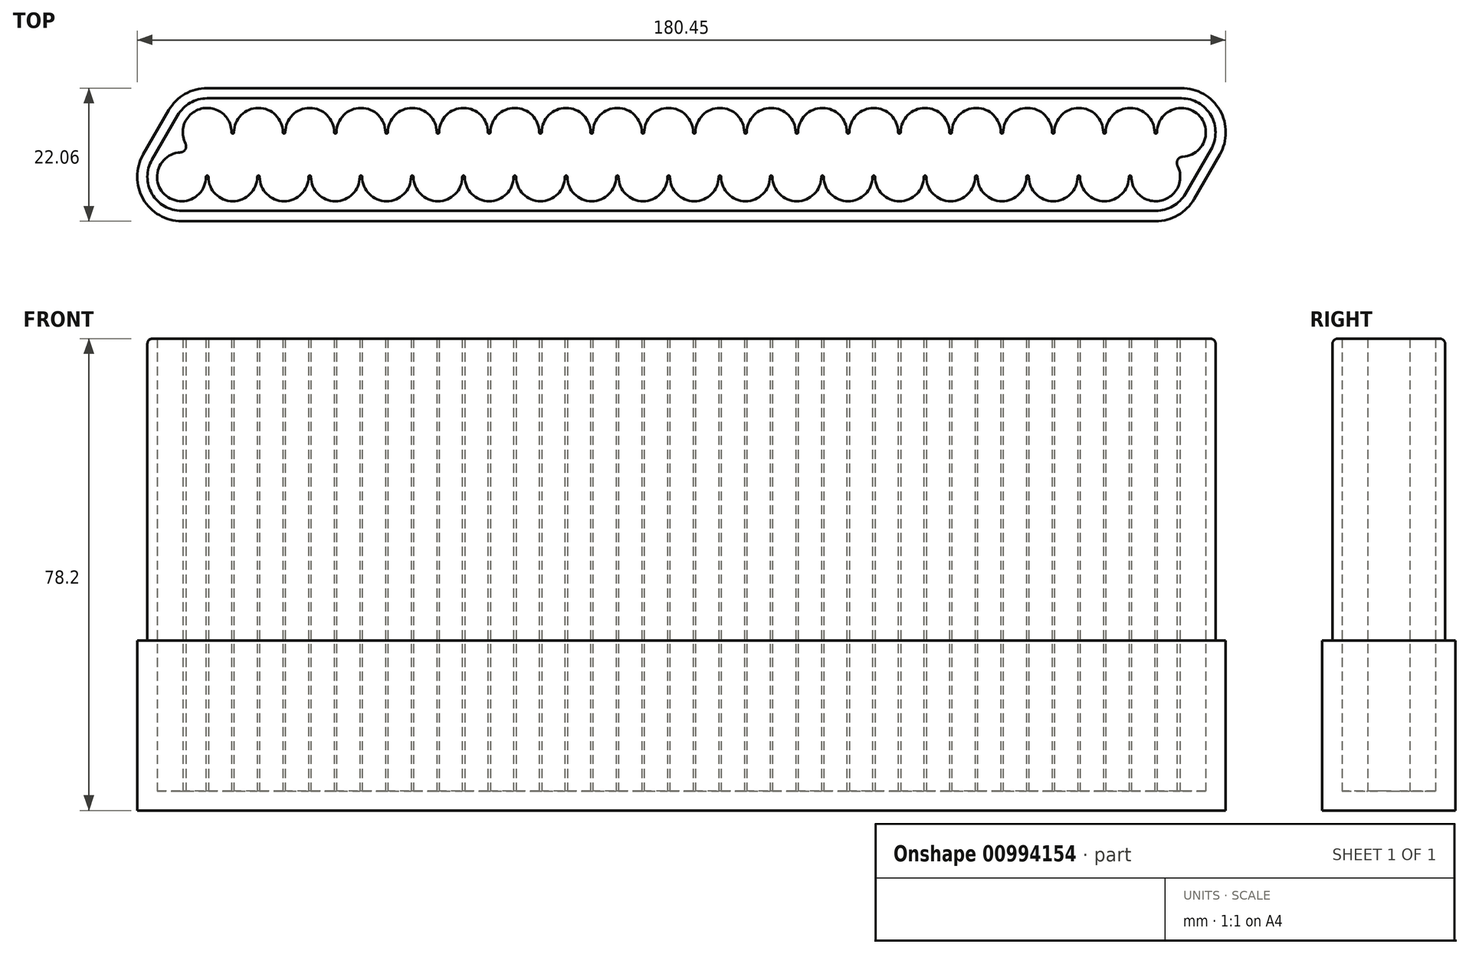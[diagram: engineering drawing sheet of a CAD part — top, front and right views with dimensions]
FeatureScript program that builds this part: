
annotation { "Feature Type Name" : "Feature", "Feature Type Description" : "" }
export const myFeature = defineFeature(function(context is Context, id is Id, definition is map)
    precondition{}
    {
        {
            var Q0;
            Q0=qCreatedBy(makeId("Top.planeOp"),FACE);
            var sketch = newSketch(context, id + "F0", { "sketchPlane" : qUnion([Q0])});
            skCircle(sketch, "E0", {"center": v(0, 0) * mm, "radius": 4.05 * mm});
            skCircle(sketch, "E1.0.1.0", {"center": v(4.25, 7.36) * mm, "radius": 4.05 * mm});
            skCircle(sketch, "E1.1.0.0", {"center": v(8.5, 0) * mm, "radius": 4.05 * mm});
            skCircle(sketch, "E1.1.1.0", {"center": v(12.75, 7.36) * mm, "radius": 4.05 * mm});
            skCircle(sketch, "E1.2.0.0", {"center": v(17, 0) * mm, "radius": 4.05 * mm});
            skCircle(sketch, "E1.2.1.0", {"center": v(21.25, 7.36) * mm, "radius": 4.05 * mm});
            skCircle(sketch, "E1.3.0.0", {"center": v(25.5, 0) * mm, "radius": 4.05 * mm});
            skCircle(sketch, "E1.3.1.0", {"center": v(29.75, 7.36) * mm, "radius": 4.05 * mm});
            skCircle(sketch, "E1.4.0.0", {"center": v(34, 0) * mm, "radius": 4.05 * mm});
            skCircle(sketch, "E1.4.1.0", {"center": v(38.25, 7.36) * mm, "radius": 4.05 * mm});
            skCircle(sketch, "E1.5.0.0", {"center": v(42.5, 0) * mm, "radius": 4.05 * mm});
            skCircle(sketch, "E1.5.1.0", {"center": v(46.75, 7.36) * mm, "radius": 4.05 * mm});
            skCircle(sketch, "E1.6.0.0", {"center": v(51, 0) * mm, "radius": 4.05 * mm});
            skCircle(sketch, "E1.6.1.0", {"center": v(55.25, 7.36) * mm, "radius": 4.05 * mm});
            skCircle(sketch, "E1.7.0.0", {"center": v(59.5, 0) * mm, "radius": 4.05 * mm});
            skCircle(sketch, "E1.7.1.0", {"center": v(63.75, 7.36) * mm, "radius": 4.05 * mm});
            skCircle(sketch, "E1.8.0.0", {"center": v(68, 0) * mm, "radius": 4.05 * mm});
            skCircle(sketch, "E1.8.1.0", {"center": v(72.25, 7.36) * mm, "radius": 4.05 * mm});
            skCircle(sketch, "E1.9.0.0", {"center": v(76.5, 0) * mm, "radius": 4.05 * mm});
            skCircle(sketch, "E1.9.1.0", {"center": v(80.75, 7.36) * mm, "radius": 4.05 * mm});
            skLineSegment(sketch, "E1.direction1", {"start": v(0, 0) * mm, "end": v(8.5, 0) * mm, "construction": true});
            skLineSegment(sketch, "E1.direction2", {"start": v(0, 0) * mm, "end": v(4.25, 7.36) * mm, "construction": true});
            skLineSegment(sketch, "E2", {"start": v(-6.37, 3.67) * mm, "end": v(-2.12, 11.04) * mm});
            skLineSegment(sketch, "E3", {"start": v(-4.9, 2.83) * mm, "end": v(-0.64, 10.19) * mm});
            skLineSegment(sketch, "E4", {"start": v(170.64, 4.54) * mm, "end": v(166.4, -2.83) * mm});
            skLineSegment(sketch, "E5", {"start": v(172.12, 3.69) * mm, "end": v(167.87, -3.68) * mm});
            skLineSegment(sketch, "E6", {"start": v(4.25, 13.01) * mm, "end": v(165.75, 13.01) * mm});
            skLineSegment(sketch, "E7", {"start": v(165.75, 14.71) * mm, "end": v(4.25, 14.71) * mm});
            skLineSegment(sketch, "E8", {"start": v(0, -5.65) * mm, "end": v(161.5, -5.65) * mm});
            skLineSegment(sketch, "E9", {"start": v(161.5, -7.35) * mm, "end": v(0, -7.35) * mm});
            skArc(sketch, "E10", {"start": v(-6.37, 3.67) * mm, "mid": v(-6.37, -3.68) * mm, "end": v(0, -7.35) * mm});
            skArc(sketch, "E11", {"start": v(0, -7.35) * mm, "mid": v(6.37, 3.68) * mm, "end": v(-6.37, 3.67) * mm, "construction": true});
            skArc(sketch, "E12", {"start": v(0, -5.65) * mm, "mid": v(4.9, 2.82) * mm, "end": v(-4.9, 2.83) * mm, "construction": true});
            skArc(sketch, "E13", {"start": v(-4.9, 2.83) * mm, "mid": v(-4.9, -2.83) * mm, "end": v(0, -5.65) * mm});
            skArc(sketch, "E14", {"start": v(4.25, 13.01) * mm, "mid": v(1.43, 12.25) * mm, "end": v(-0.64, 10.19) * mm});
            skArc(sketch, "E15", {"start": v(-0.64, 10.19) * mm, "mid": v(7.08, 2.47) * mm, "end": v(4.25, 13.01) * mm, "construction": true});
            skArc(sketch, "E16", {"start": v(-2.12, 11.04) * mm, "mid": v(7.93, 1) * mm, "end": v(4.25, 14.71) * mm, "construction": true});
            skArc(sketch, "E17", {"start": v(4.25, 14.71) * mm, "mid": v(0.58, 13.73) * mm, "end": v(-2.12, 11.04) * mm});
            skArc(sketch, "E18", {"start": v(165.75, 14.71) * mm, "mid": v(159.38, 3.69) * mm, "end": v(172.12, 3.69) * mm, "construction": true});
            skArc(sketch, "E19", {"start": v(172.12, 3.69) * mm, "mid": v(172.12, 11.04) * mm, "end": v(165.75, 14.71) * mm});
            skArc(sketch, "E20", {"start": v(170.64, 4.54) * mm, "mid": v(170.64, 10.19) * mm, "end": v(165.75, 13.01) * mm});
            skArc(sketch, "E21", {"start": v(165.75, 13.01) * mm, "mid": v(160.86, 4.54) * mm, "end": v(170.64, 4.54) * mm, "construction": true});
            skArc(sketch, "E22", {"start": v(167.87, -3.68) * mm, "mid": v(157.83, 6.37) * mm, "end": v(161.5, -7.35) * mm, "construction": true});
            skArc(sketch, "E23", {"start": v(161.5, -7.35) * mm, "mid": v(165.17, -6.37) * mm, "end": v(167.87, -3.68) * mm});
            skArc(sketch, "E24", {"start": v(161.5, -5.65) * mm, "mid": v(164.32, -4.9) * mm, "end": v(166.4, -2.83) * mm});
            skArc(sketch, "E25", {"start": v(166.4, -2.82) * mm, "mid": v(158.67, 4.9) * mm, "end": v(161.5, -5.65) * mm, "construction": true});
            skArc(sketch, "E26", {"start": v(4.45, 0) * mm, "mid": v(4.25, 0.2) * mm, "end": v(4.05, 0) * mm});
            skArc(sketch, "E27", {"start": v(4.05, 0) * mm, "mid": v(4.25, -0.2) * mm, "end": v(4.45, 0) * mm});
            skArc(sketch, "E28.0.1.0", {"start": v(8.7, 7.36) * mm, "mid": v(8.5, 7.56) * mm, "end": v(8.3, 7.36) * mm});
            skArc(sketch, "E28.0.1.1", {"start": v(8.3, 7.36) * mm, "mid": v(8.5, 7.16) * mm, "end": v(8.7, 7.36) * mm});
            skArc(sketch, "E28.1.0.0", {"start": v(12.95, 0) * mm, "mid": v(12.75, 0.2) * mm, "end": v(12.55, 0) * mm});
            skArc(sketch, "E28.1.0.1", {"start": v(12.55, 0) * mm, "mid": v(12.75, -0.2) * mm, "end": v(12.95, 0) * mm});
            skArc(sketch, "E28.1.1.0", {"start": v(17.2, 7.36) * mm, "mid": v(17, 7.56) * mm, "end": v(16.8, 7.36) * mm});
            skArc(sketch, "E28.1.1.1", {"start": v(16.8, 7.36) * mm, "mid": v(17, 7.16) * mm, "end": v(17.2, 7.36) * mm});
            skArc(sketch, "E28.2.0.0", {"start": v(21.45, 0) * mm, "mid": v(21.25, 0.2) * mm, "end": v(21.05, 0) * mm});
            skArc(sketch, "E28.2.0.1", {"start": v(21.05, 0) * mm, "mid": v(21.25, -0.2) * mm, "end": v(21.45, 0) * mm});
            skArc(sketch, "E28.2.1.0", {"start": v(25.7, 7.36) * mm, "mid": v(25.5, 7.56) * mm, "end": v(25.3, 7.36) * mm});
            skArc(sketch, "E28.2.1.1", {"start": v(25.3, 7.36) * mm, "mid": v(25.5, 7.16) * mm, "end": v(25.7, 7.36) * mm});
            skLineSegment(sketch, "E28.direction1", {"start": v(4.25, 0) * mm, "end": v(12.75, 0) * mm, "construction": true});
            skLineSegment(sketch, "E28.direction2", {"start": v(4.25, 0) * mm, "end": v(8.5, 7.36) * mm, "construction": true});
            skCircle(sketch, "E29.0.10.0", {"center": v(85, 0) * mm, "radius": 4.05 * mm});
            skCircle(sketch, "E29.0.10.1", {"center": v(89.25, 7.36) * mm, "radius": 4.05 * mm});
            skCircle(sketch, "E29.0.11.0", {"center": v(93.5, 0) * mm, "radius": 4.05 * mm});
            skCircle(sketch, "E29.0.11.1", {"center": v(97.75, 7.36) * mm, "radius": 4.05 * mm});
            skCircle(sketch, "E29.0.12.0", {"center": v(102, 0) * mm, "radius": 4.05 * mm});
            skCircle(sketch, "E29.0.12.1", {"center": v(106.25, 7.36) * mm, "radius": 4.05 * mm});
            skCircle(sketch, "E29.0.13.0", {"center": v(110.5, 0) * mm, "radius": 4.05 * mm});
            skCircle(sketch, "E29.0.13.1", {"center": v(114.75, 7.36) * mm, "radius": 4.05 * mm});
            skCircle(sketch, "E29.0.14.0", {"center": v(119, 0) * mm, "radius": 4.05 * mm});
            skCircle(sketch, "E29.0.14.1", {"center": v(123.25, 7.36) * mm, "radius": 4.05 * mm});
            skCircle(sketch, "E29.0.15.0", {"center": v(127.5, 0) * mm, "radius": 4.05 * mm});
            skCircle(sketch, "E29.0.15.1", {"center": v(131.75, 7.36) * mm, "radius": 4.05 * mm});
            skCircle(sketch, "E29.0.16.0", {"center": v(136, 0) * mm, "radius": 4.05 * mm});
            skCircle(sketch, "E29.0.16.1", {"center": v(140.25, 7.36) * mm, "radius": 4.05 * mm});
            skCircle(sketch, "E29.0.17.0", {"center": v(144.5, 0) * mm, "radius": 4.05 * mm});
            skCircle(sketch, "E29.0.17.1", {"center": v(148.75, 7.36) * mm, "radius": 4.05 * mm});
            skCircle(sketch, "E29.0.18.0", {"center": v(153, 0) * mm, "radius": 4.05 * mm});
            skCircle(sketch, "E29.0.18.1", {"center": v(157.25, 7.36) * mm, "radius": 4.05 * mm});
            skCircle(sketch, "E29.0.19.0", {"center": v(161.5, 0) * mm, "radius": 4.05 * mm});
            skCircle(sketch, "E29.0.19.1", {"center": v(165.75, 7.36) * mm, "radius": 4.05 * mm});
            skArc(sketch, "E30.0.3.0", {"start": v(29.95, 0) * mm, "mid": v(29.75, 0.2) * mm, "end": v(29.55, 0) * mm});
            skArc(sketch, "E30.4.3.0", {"start": v(29.55, 0) * mm, "mid": v(29.75, -0.2) * mm, "end": v(29.95, 0) * mm});
            skArc(sketch, "E30.0.3.1", {"start": v(34.2, 7.36) * mm, "mid": v(34, 7.56) * mm, "end": v(33.8, 7.36) * mm});
            skArc(sketch, "E30.4.3.1", {"start": v(33.8, 7.36) * mm, "mid": v(34, 7.16) * mm, "end": v(34.2, 7.36) * mm});
            skArc(sketch, "E30.0.4.0", {"start": v(38.45, 0) * mm, "mid": v(38.25, 0.2) * mm, "end": v(38.05, 0) * mm});
            skArc(sketch, "E30.4.4.0", {"start": v(38.05, 0) * mm, "mid": v(38.25, -0.2) * mm, "end": v(38.45, 0) * mm});
            skArc(sketch, "E30.0.4.1", {"start": v(42.7, 7.36) * mm, "mid": v(42.5, 7.56) * mm, "end": v(42.3, 7.36) * mm});
            skArc(sketch, "E30.4.4.1", {"start": v(42.3, 7.36) * mm, "mid": v(42.5, 7.16) * mm, "end": v(42.7, 7.36) * mm});
            skArc(sketch, "E30.0.5.0", {"start": v(46.95, 0) * mm, "mid": v(46.75, 0.2) * mm, "end": v(46.55, 0) * mm});
            skArc(sketch, "E30.4.5.0", {"start": v(46.55, 0) * mm, "mid": v(46.75, -0.2) * mm, "end": v(46.95, 0) * mm});
            skArc(sketch, "E30.0.5.1", {"start": v(51.2, 7.36) * mm, "mid": v(51, 7.56) * mm, "end": v(50.8, 7.36) * mm});
            skArc(sketch, "E30.4.5.1", {"start": v(50.8, 7.36) * mm, "mid": v(51, 7.16) * mm, "end": v(51.2, 7.36) * mm});
            skArc(sketch, "E30.0.6.0", {"start": v(55.45, 0) * mm, "mid": v(55.25, 0.2) * mm, "end": v(55.05, 0) * mm});
            skArc(sketch, "E30.4.6.0", {"start": v(55.05, 0) * mm, "mid": v(55.25, -0.2) * mm, "end": v(55.45, 0) * mm});
            skArc(sketch, "E30.0.6.1", {"start": v(59.7, 7.36) * mm, "mid": v(59.5, 7.56) * mm, "end": v(59.3, 7.36) * mm});
            skArc(sketch, "E30.4.6.1", {"start": v(59.3, 7.36) * mm, "mid": v(59.5, 7.16) * mm, "end": v(59.7, 7.36) * mm});
            skArc(sketch, "E30.0.7.0", {"start": v(63.95, 0) * mm, "mid": v(63.75, 0.2) * mm, "end": v(63.55, 0) * mm});
            skArc(sketch, "E30.4.7.0", {"start": v(63.55, 0) * mm, "mid": v(63.75, -0.2) * mm, "end": v(63.95, 0) * mm});
            skArc(sketch, "E30.0.7.1", {"start": v(68.2, 7.36) * mm, "mid": v(68, 7.56) * mm, "end": v(67.8, 7.36) * mm});
            skArc(sketch, "E30.4.7.1", {"start": v(67.8, 7.36) * mm, "mid": v(68, 7.16) * mm, "end": v(68.2, 7.36) * mm});
            skArc(sketch, "E30.0.8.0", {"start": v(72.45, 0) * mm, "mid": v(72.25, 0.2) * mm, "end": v(72.05, 0) * mm});
            skArc(sketch, "E30.4.8.0", {"start": v(72.05, 0) * mm, "mid": v(72.25, -0.2) * mm, "end": v(72.45, 0) * mm});
            skArc(sketch, "E30.0.8.1", {"start": v(76.7, 7.36) * mm, "mid": v(76.5, 7.56) * mm, "end": v(76.3, 7.36) * mm});
            skArc(sketch, "E30.4.8.1", {"start": v(76.3, 7.36) * mm, "mid": v(76.5, 7.16) * mm, "end": v(76.7, 7.36) * mm});
            skArc(sketch, "E30.0.9.0", {"start": v(80.95, 0) * mm, "mid": v(80.75, 0.2) * mm, "end": v(80.55, 0) * mm});
            skArc(sketch, "E30.4.9.0", {"start": v(80.55, 0) * mm, "mid": v(80.75, -0.2) * mm, "end": v(80.95, 0) * mm});
            skArc(sketch, "E30.0.9.1", {"start": v(85.2, 7.36) * mm, "mid": v(85, 7.56) * mm, "end": v(84.8, 7.36) * mm});
            skArc(sketch, "E30.4.9.1", {"start": v(84.8, 7.36) * mm, "mid": v(85, 7.16) * mm, "end": v(85.2, 7.36) * mm});
            skArc(sketch, "E30.0.10.0", {"start": v(89.45, 0) * mm, "mid": v(89.25, 0.2) * mm, "end": v(89.05, 0) * mm});
            skArc(sketch, "E30.4.10.0", {"start": v(89.05, 0) * mm, "mid": v(89.25, -0.2) * mm, "end": v(89.45, 0) * mm});
            skArc(sketch, "E30.0.10.1", {"start": v(93.7, 7.36) * mm, "mid": v(93.5, 7.56) * mm, "end": v(93.3, 7.36) * mm});
            skArc(sketch, "E30.4.10.1", {"start": v(93.3, 7.36) * mm, "mid": v(93.5, 7.16) * mm, "end": v(93.7, 7.36) * mm});
            skArc(sketch, "E30.0.11.0", {"start": v(97.95, 0) * mm, "mid": v(97.75, 0.2) * mm, "end": v(97.55, 0) * mm});
            skArc(sketch, "E30.4.11.0", {"start": v(97.55, 0) * mm, "mid": v(97.75, -0.2) * mm, "end": v(97.95, 0) * mm});
            skArc(sketch, "E30.0.11.1", {"start": v(102.2, 7.36) * mm, "mid": v(102, 7.56) * mm, "end": v(101.8, 7.36) * mm});
            skArc(sketch, "E30.4.11.1", {"start": v(101.8, 7.36) * mm, "mid": v(102, 7.16) * mm, "end": v(102.2, 7.36) * mm});
            skArc(sketch, "E30.0.12.0", {"start": v(106.45, 0) * mm, "mid": v(106.25, 0.2) * mm, "end": v(106.05, 0) * mm});
            skArc(sketch, "E30.4.12.0", {"start": v(106.05, 0) * mm, "mid": v(106.25, -0.2) * mm, "end": v(106.45, 0) * mm});
            skArc(sketch, "E30.0.12.1", {"start": v(110.7, 7.36) * mm, "mid": v(110.5, 7.56) * mm, "end": v(110.3, 7.36) * mm});
            skArc(sketch, "E30.4.12.1", {"start": v(110.3, 7.36) * mm, "mid": v(110.5, 7.16) * mm, "end": v(110.7, 7.36) * mm});
            skArc(sketch, "E30.0.13.0", {"start": v(114.95, 0) * mm, "mid": v(114.75, 0.2) * mm, "end": v(114.55, 0) * mm});
            skArc(sketch, "E30.4.13.0", {"start": v(114.55, 0) * mm, "mid": v(114.75, -0.2) * mm, "end": v(114.95, 0) * mm});
            skArc(sketch, "E30.0.13.1", {"start": v(119.2, 7.36) * mm, "mid": v(119, 7.56) * mm, "end": v(118.8, 7.36) * mm});
            skArc(sketch, "E30.4.13.1", {"start": v(118.8, 7.36) * mm, "mid": v(119, 7.16) * mm, "end": v(119.2, 7.36) * mm});
            skArc(sketch, "E30.0.14.0", {"start": v(123.45, 0) * mm, "mid": v(123.25, 0.2) * mm, "end": v(123.05, 0) * mm});
            skArc(sketch, "E30.4.14.0", {"start": v(123.05, 0) * mm, "mid": v(123.25, -0.2) * mm, "end": v(123.45, 0) * mm});
            skArc(sketch, "E30.0.14.1", {"start": v(127.7, 7.36) * mm, "mid": v(127.5, 7.56) * mm, "end": v(127.3, 7.36) * mm});
            skArc(sketch, "E30.4.14.1", {"start": v(127.3, 7.36) * mm, "mid": v(127.5, 7.16) * mm, "end": v(127.7, 7.36) * mm});
            skArc(sketch, "E30.0.15.0", {"start": v(131.95, 0) * mm, "mid": v(131.75, 0.2) * mm, "end": v(131.55, 0) * mm});
            skArc(sketch, "E30.4.15.0", {"start": v(131.55, 0) * mm, "mid": v(131.75, -0.2) * mm, "end": v(131.95, 0) * mm});
            skArc(sketch, "E30.0.15.1", {"start": v(136.2, 7.36) * mm, "mid": v(136, 7.56) * mm, "end": v(135.8, 7.36) * mm});
            skArc(sketch, "E30.4.15.1", {"start": v(135.8, 7.36) * mm, "mid": v(136, 7.16) * mm, "end": v(136.2, 7.36) * mm});
            skArc(sketch, "E30.0.16.0", {"start": v(140.45, 0) * mm, "mid": v(140.25, 0.2) * mm, "end": v(140.05, 0) * mm});
            skArc(sketch, "E30.4.16.0", {"start": v(140.05, 0) * mm, "mid": v(140.25, -0.2) * mm, "end": v(140.45, 0) * mm});
            skArc(sketch, "E30.0.16.1", {"start": v(144.7, 7.36) * mm, "mid": v(144.5, 7.56) * mm, "end": v(144.3, 7.36) * mm});
            skArc(sketch, "E30.4.16.1", {"start": v(144.3, 7.36) * mm, "mid": v(144.5, 7.16) * mm, "end": v(144.7, 7.36) * mm});
            skArc(sketch, "E30.0.17.0", {"start": v(148.95, 0) * mm, "mid": v(148.75, 0.2) * mm, "end": v(148.55, 0) * mm});
            skArc(sketch, "E30.4.17.0", {"start": v(148.55, 0) * mm, "mid": v(148.75, -0.2) * mm, "end": v(148.95, 0) * mm});
            skArc(sketch, "E30.0.17.1", {"start": v(153.2, 7.36) * mm, "mid": v(153, 7.56) * mm, "end": v(152.8, 7.36) * mm});
            skArc(sketch, "E30.4.17.1", {"start": v(152.8, 7.36) * mm, "mid": v(153, 7.16) * mm, "end": v(153.2, 7.36) * mm});
            skArc(sketch, "E30.0.18.0", {"start": v(157.45, 0) * mm, "mid": v(157.25, 0.2) * mm, "end": v(157.05, 0) * mm});
            skArc(sketch, "E30.4.18.0", {"start": v(157.05, 0) * mm, "mid": v(157.25, -0.2) * mm, "end": v(157.45, 0) * mm});
            skArc(sketch, "E30.0.18.1", {"start": v(161.7, 7.36) * mm, "mid": v(161.5, 7.56) * mm, "end": v(161.3, 7.36) * mm});
            skArc(sketch, "E30.4.18.1", {"start": v(161.3, 7.36) * mm, "mid": v(161.5, 7.16) * mm, "end": v(161.7, 7.36) * mm});
            skLineSegment(sketch, "E31", {"start": v(161.5, 0) * mm, "end": v(165.75, 7.36) * mm, "construction": true});
            skLineSegment(sketch, "E32", {"start": v(2.13, 3.68) * mm, "end": v(-0.24, 5.04) * mm, "construction": true});
            skArc(sketch, "E33", {"start": v(0.65, 5.5) * mm, "mid": v(-1.1, 5.54) * mm, "end": v(-0.2, 4.05) * mm, "construction": true});
            skArc(sketch, "E34", {"start": v(-0.2, 4.05) * mm, "mid": v(0.63, 4.54) * mm, "end": v(0.65, 5.5) * mm});
            skLineSegment(sketch, "E35", {"start": v(163.62, 3.68) * mm, "end": v(165.99, 2.32) * mm, "construction": true});
            skArc(sketch, "E36", {"start": v(165.94, 3.32) * mm, "mid": v(165.12, 2.82) * mm, "end": v(165.1, 1.86) * mm});
            skArc(sketch, "E37", {"start": v(165.1, 1.86) * mm, "mid": v(166.85, 1.82) * mm, "end": v(165.94, 3.32) * mm, "construction": true});
            skSolve(sketch);
        }
        {
            var Q0;
            Q0=makeQuery(id+"F0.imprint","IMPRINT",FACE,{"disambiguationData":[TD([[makeQuery(id+"F0.imprint","IMPRINT",EDGE,{"derivedFrom":sQuery(id+"F0.wireOp",EDGE,"E3")}),-1.0]])]});
            var Q1;
            Q1=makeQuery(id+"F0.imprint","IMPRINT",FACE,{"disambiguationData":[TD([[makeQuery(id+"F0.imprint","IMPRINT",EDGE,{"derivedFrom":sQuery(id+"F0.wireOp",EDGE,"E26")}),1.0]])]});
            var Q2;
            {var subQ0=sQuery(id+"F0.wireOp",EDGE,"E28.0.1.0");Q2=makeQuery(id+"F0.imprint","IMPRINT",FACE,{"disambiguationData":[TD([[makeQuery(id+"F0.imprint","IMPRINT",EDGE,{"derivedFrom":subQ0}),1.0]])]});}
            var Q3;
            Q3=makeQuery(id+"F0.imprint","IMPRINT",FACE,{"disambiguationData":[TD([[makeQuery(id+"F0.imprint","IMPRINT",EDGE,{"derivedFrom":sQuery(id+"F0.wireOp",EDGE,"E28.1.0.0")}),1.0]])]});
            var Q4;
            Q4=makeQuery(id+"F0.imprint","IMPRINT",FACE,{"disambiguationData":[TD([[makeQuery(id+"F0.imprint","IMPRINT",EDGE,{"derivedFrom":sQuery(id+"F0.wireOp",EDGE,"E28.1.1.0")}),1.0]])]});
            var Q5;
            Q5=makeQuery(id+"F0.imprint","IMPRINT",FACE,{"disambiguationData":[TD([[makeQuery(id+"F0.imprint","IMPRINT",EDGE,{"derivedFrom":sQuery(id+"F0.wireOp",EDGE,"E28.2.0.0")}),1.0]])]});
            var Q6;
            Q6=makeQuery(id+"F0.imprint","IMPRINT",FACE,{"disambiguationData":[TD([[makeQuery(id+"F0.imprint","IMPRINT",EDGE,{"derivedFrom":sQuery(id+"F0.wireOp",EDGE,"E28.2.1.0")}),1.0]])]});
            var Q7;
            Q7=makeQuery(id+"F0.imprint","IMPRINT",FACE,{"disambiguationData":[TD([[makeQuery(id+"F0.imprint","IMPRINT",EDGE,{"derivedFrom":sQuery(id+"F0.wireOp",EDGE,"E30.0.3.0")}),1.0]])]});
            var Q8;
            Q8=makeQuery(id+"F0.imprint","IMPRINT",FACE,{"disambiguationData":[TD([[makeQuery(id+"F0.imprint","IMPRINT",EDGE,{"derivedFrom":sQuery(id+"F0.wireOp",EDGE,"E30.0.3.1")}),1.0]])]});
            var Q9;
            Q9=makeQuery(id+"F0.imprint","IMPRINT",FACE,{"disambiguationData":[TD([[makeQuery(id+"F0.imprint","IMPRINT",EDGE,{"derivedFrom":sQuery(id+"F0.wireOp",EDGE,"E30.0.4.0")}),1.0]])]});
            var Q10;
            Q10=makeQuery(id+"F0.imprint","IMPRINT",FACE,{"disambiguationData":[TD([[makeQuery(id+"F0.imprint","IMPRINT",EDGE,{"derivedFrom":sQuery(id+"F0.wireOp",EDGE,"E30.0.4.1")}),1.0]])]});
            var Q11;
            Q11=makeQuery(id+"F0.imprint","IMPRINT",FACE,{"disambiguationData":[TD([[makeQuery(id+"F0.imprint","IMPRINT",EDGE,{"derivedFrom":sQuery(id+"F0.wireOp",EDGE,"E30.0.5.0")}),1.0]])]});
            var Q12;
            Q12=makeQuery(id+"F0.imprint","IMPRINT",FACE,{"disambiguationData":[TD([[makeQuery(id+"F0.imprint","IMPRINT",EDGE,{"derivedFrom":sQuery(id+"F0.wireOp",EDGE,"E30.0.5.1")}),1.0]])]});
            var Q13;
            Q13=makeQuery(id+"F0.imprint","IMPRINT",FACE,{"disambiguationData":[TD([[makeQuery(id+"F0.imprint","IMPRINT",EDGE,{"derivedFrom":sQuery(id+"F0.wireOp",EDGE,"E30.0.6.0")}),1.0]])]});
            var Q14;
            Q14=makeQuery(id+"F0.imprint","IMPRINT",FACE,{"disambiguationData":[TD([[makeQuery(id+"F0.imprint","IMPRINT",EDGE,{"derivedFrom":sQuery(id+"F0.wireOp",EDGE,"E30.0.6.1")}),1.0]])]});
            var Q15;
            Q15=makeQuery(id+"F0.imprint","IMPRINT",FACE,{"disambiguationData":[TD([[makeQuery(id+"F0.imprint","IMPRINT",EDGE,{"derivedFrom":sQuery(id+"F0.wireOp",EDGE,"E30.0.7.0")}),1.0]])]});
            var Q16;
            Q16=makeQuery(id+"F0.imprint","IMPRINT",FACE,{"disambiguationData":[TD([[makeQuery(id+"F0.imprint","IMPRINT",EDGE,{"derivedFrom":sQuery(id+"F0.wireOp",EDGE,"E30.0.7.1")}),1.0]])]});
            var Q17;
            Q17=makeQuery(id+"F0.imprint","IMPRINT",FACE,{"disambiguationData":[TD([[makeQuery(id+"F0.imprint","IMPRINT",EDGE,{"derivedFrom":sQuery(id+"F0.wireOp",EDGE,"E30.0.8.0")}),1.0]])]});
            var Q18;
            Q18=makeQuery(id+"F0.imprint","IMPRINT",FACE,{"disambiguationData":[TD([[makeQuery(id+"F0.imprint","IMPRINT",EDGE,{"derivedFrom":sQuery(id+"F0.wireOp",EDGE,"E30.0.8.1")}),1.0]])]});
            var Q19;
            Q19=makeQuery(id+"F0.imprint","IMPRINT",FACE,{"disambiguationData":[TD([[makeQuery(id+"F0.imprint","IMPRINT",EDGE,{"derivedFrom":sQuery(id+"F0.wireOp",EDGE,"E30.0.9.0")}),1.0]])]});
            var Q20;
            Q20=makeQuery(id+"F0.imprint","IMPRINT",FACE,{"disambiguationData":[TD([[makeQuery(id+"F0.imprint","IMPRINT",EDGE,{"derivedFrom":sQuery(id+"F0.wireOp",EDGE,"E30.0.9.1")}),1.0]])]});
            var Q21;
            Q21=makeQuery(id+"F0.imprint","IMPRINT",FACE,{"disambiguationData":[TD([[makeQuery(id+"F0.imprint","IMPRINT",EDGE,{"derivedFrom":sQuery(id+"F0.wireOp",EDGE,"E30.0.10.0")}),1.0]])]});
            var Q22;
            Q22=makeQuery(id+"F0.imprint","IMPRINT",FACE,{"disambiguationData":[TD([[makeQuery(id+"F0.imprint","IMPRINT",EDGE,{"derivedFrom":sQuery(id+"F0.wireOp",EDGE,"E30.0.10.1")}),1.0]])]});
            var Q23;
            Q23=makeQuery(id+"F0.imprint","IMPRINT",FACE,{"disambiguationData":[TD([[makeQuery(id+"F0.imprint","IMPRINT",EDGE,{"derivedFrom":sQuery(id+"F0.wireOp",EDGE,"E30.0.11.0")}),1.0]])]});
            var Q24;
            Q24=makeQuery(id+"F0.imprint","IMPRINT",FACE,{"disambiguationData":[TD([[makeQuery(id+"F0.imprint","IMPRINT",EDGE,{"derivedFrom":sQuery(id+"F0.wireOp",EDGE,"E30.0.11.1")}),1.0]])]});
            var Q25;
            Q25=makeQuery(id+"F0.imprint","IMPRINT",FACE,{"disambiguationData":[TD([[makeQuery(id+"F0.imprint","IMPRINT",EDGE,{"derivedFrom":sQuery(id+"F0.wireOp",EDGE,"E30.0.12.0")}),1.0]])]});
            var Q26;
            Q26=makeQuery(id+"F0.imprint","IMPRINT",FACE,{"disambiguationData":[TD([[makeQuery(id+"F0.imprint","IMPRINT",EDGE,{"derivedFrom":sQuery(id+"F0.wireOp",EDGE,"E30.0.12.1")}),1.0]])]});
            var Q27;
            Q27=makeQuery(id+"F0.imprint","IMPRINT",FACE,{"disambiguationData":[TD([[makeQuery(id+"F0.imprint","IMPRINT",EDGE,{"derivedFrom":sQuery(id+"F0.wireOp",EDGE,"E30.0.13.0")}),1.0]])]});
            var Q28;
            Q28=makeQuery(id+"F0.imprint","IMPRINT",FACE,{"disambiguationData":[TD([[makeQuery(id+"F0.imprint","IMPRINT",EDGE,{"derivedFrom":sQuery(id+"F0.wireOp",EDGE,"E30.0.13.1")}),1.0]])]});
            var Q29;
            Q29=makeQuery(id+"F0.imprint","IMPRINT",FACE,{"disambiguationData":[TD([[makeQuery(id+"F0.imprint","IMPRINT",EDGE,{"derivedFrom":sQuery(id+"F0.wireOp",EDGE,"E30.0.14.0")}),1.0]])]});
            var Q30;
            Q30=makeQuery(id+"F0.imprint","IMPRINT",FACE,{"disambiguationData":[TD([[makeQuery(id+"F0.imprint","IMPRINT",EDGE,{"derivedFrom":sQuery(id+"F0.wireOp",EDGE,"E30.0.14.1")}),1.0]])]});
            var Q31;
            Q31=makeQuery(id+"F0.imprint","IMPRINT",FACE,{"disambiguationData":[TD([[makeQuery(id+"F0.imprint","IMPRINT",EDGE,{"derivedFrom":sQuery(id+"F0.wireOp",EDGE,"E30.0.15.0")}),1.0]])]});
            var Q32;
            Q32=makeQuery(id+"F0.imprint","IMPRINT",FACE,{"disambiguationData":[TD([[makeQuery(id+"F0.imprint","IMPRINT",EDGE,{"derivedFrom":sQuery(id+"F0.wireOp",EDGE,"E30.0.15.1")}),1.0]])]});
            var Q33;
            Q33=makeQuery(id+"F0.imprint","IMPRINT",FACE,{"disambiguationData":[TD([[makeQuery(id+"F0.imprint","IMPRINT",EDGE,{"derivedFrom":sQuery(id+"F0.wireOp",EDGE,"E30.0.16.0")}),1.0]])]});
            var Q34;
            Q34=makeQuery(id+"F0.imprint","IMPRINT",FACE,{"disambiguationData":[TD([[makeQuery(id+"F0.imprint","IMPRINT",EDGE,{"derivedFrom":sQuery(id+"F0.wireOp",EDGE,"E30.0.16.1")}),1.0]])]});
            var Q35;
            Q35=makeQuery(id+"F0.imprint","IMPRINT",FACE,{"disambiguationData":[TD([[makeQuery(id+"F0.imprint","IMPRINT",EDGE,{"derivedFrom":sQuery(id+"F0.wireOp",EDGE,"E30.0.17.0")}),1.0]])]});
            var Q36;
            Q36=makeQuery(id+"F0.imprint","IMPRINT",FACE,{"disambiguationData":[TD([[makeQuery(id+"F0.imprint","IMPRINT",EDGE,{"derivedFrom":sQuery(id+"F0.wireOp",EDGE,"E30.0.17.1")}),1.0]])]});
            var Q37;
            Q37=makeQuery(id+"F0.imprint","IMPRINT",FACE,{"disambiguationData":[TD([[makeQuery(id+"F0.imprint","IMPRINT",EDGE,{"derivedFrom":sQuery(id+"F0.wireOp",EDGE,"E30.0.18.0")}),1.0]])]});
            var Q38;
            Q38=makeQuery(id+"F0.imprint","IMPRINT",FACE,{"disambiguationData":[TD([[makeQuery(id+"F0.imprint","IMPRINT",EDGE,{"derivedFrom":sQuery(id+"F0.wireOp",EDGE,"E30.0.18.1")}),1.0]])]});
            extrude(context, id + "F1", {"entities" : qUnion([Q0, Q1, Q2, Q3, Q4, Q5, Q6, Q7, Q8, Q9, Q10, Q11, Q12, Q13, Q14, Q15, Q16, Q17, Q18, Q19, Q20, Q21, Q22, Q23, Q24, Q25, Q26, Q27, Q28, Q29, Q30, Q31, Q32, Q33, Q34, Q35, Q36, Q37, Q38]), "depth" : 75 * mm, "offsetDistance" : 25 * mm});
        }
        {
            var Q0;
            Q0=makeQuery(id+"F0.imprint","IMPRINT",FACE,{"disambiguationData":[TD([[makeQuery(id+"F0.imprint","IMPRINT",EDGE,{"derivedFrom":sQuery(id+"F0.wireOp",EDGE,"a81a9441-913f-4e04-ae89-87223a70fdbe.0")}),1.0]])]});
            var Q1;
            Q1=makeQuery(id+"F0.imprint","IMPRINT",FACE,{"disambiguationData":[TD([[makeQuery(id+"F0.imprint","IMPRINT",EDGE,{"derivedFrom":sQuery(id+"F0.wireOp",EDGE,"E2")}),-1.0]])]});
            extrude(context, id + "F2", {"entities" : qUnion([Q0, Q1]), "operationType" : NewBodyOperationType.ADD, "depth" : 25 * mm, "offsetDistance" : 25 * mm});
        }
        {
            var Q0;
            Q0 = qSketchRegion(id + "F0", true);
            var Q1;
            Q1=makeQuery(id+"F0.imprint","IMPRINT",FACE,{"disambiguationData":[TD([[makeQuery(id+"F0.imprint","IMPRINT",EDGE,{"derivedFrom":sQuery(id+"F0.wireOp",EDGE,"E3")}),-1.0]])]});
            var Q2;
            {var subQ50=sQuery(id+"F0.wireOp",EDGE,"f7ba4f12-d8f7-416d-8bb5-9bc70fdc84212");Q2=makeQuery(id+"F0.imprint","IMPRINT",FACE,{"disambiguationData":[TD([[makeQuery(id+"F0.imprint","IMPRINT",EDGE,{"derivedFrom":subQ50}),-1.0]])]});}
            var Q3;
            {var subQ0=sQuery(id+"F0.wireOp",EDGE,"E0");var subQ1=makeQuery(id+"F0.imprint","INTERSECT",VERTEX,{"derivedFrom":[subQ0,sQuery(id+"F0.wireOp",EDGE,"f7ba4f12-d8f7-416d-8bb5-9bc70fdc84212")]});Q3=makeQuery(id+"F0.imprint","IMPRINT",FACE,{"disambiguationData":[TD([[makeQuery(id+"F0.imprint","IMPRINT",EDGE,{"disambiguationData":[TD([[subQ1,1.0]])],"derivedFrom":subQ0}),1.0]])]});}
            var Q4;
            {var subQ0=sQuery(id+"F0.wireOp",EDGE,"E1.0.1.0");var subQ1=makeQuery(id+"F0.imprint","INTERSECT",VERTEX,{"derivedFrom":[subQ0,sQuery(id+"F0.wireOp",EDGE,"f7ba4f12-d8f7-416d-8bb5-9bc70fdc84212")]});Q4=makeQuery(id+"F0.imprint","IMPRINT",FACE,{"disambiguationData":[TD([[makeQuery(id+"F0.imprint","IMPRINT",EDGE,{"disambiguationData":[TD([[subQ1,1.0]])],"derivedFrom":subQ0}),1.0]])]});}
            var Q5;
            {var subQ0=sQuery(id+"F0.wireOp",EDGE,"E1.1.0.0");var subQ1=makeQuery(id+"F0.imprint","INTERSECT",VERTEX,{"derivedFrom":[subQ0,sQuery(id+"F0.wireOp",EDGE,"E26")]});Q5=makeQuery(id+"F0.imprint","IMPRINT",FACE,{"disambiguationData":[TD([[makeQuery(id+"F0.imprint","IMPRINT",EDGE,{"disambiguationData":[TD([[subQ1,1.0]])],"derivedFrom":subQ0}),1.0]])]});}
            var Q6;
            {var subQ0=sQuery(id+"F0.wireOp",EDGE,"E1.1.1.0");var subQ1=makeQuery(id+"F0.imprint","INTERSECT",VERTEX,{"derivedFrom":[subQ0,sQuery(id+"F0.wireOp",EDGE,"E28.0.1.1")]});Q6=makeQuery(id+"F0.imprint","IMPRINT",FACE,{"disambiguationData":[TD([[makeQuery(id+"F0.imprint","IMPRINT",EDGE,{"disambiguationData":[TD([[subQ1,1.0]])],"derivedFrom":subQ0}),1.0]])]});}
            var Q7;
            {var subQ0=sQuery(id+"F0.wireOp",EDGE,"E1.2.0.0");var subQ1=makeQuery(id+"F0.imprint","INTERSECT",VERTEX,{"derivedFrom":[subQ0,sQuery(id+"F0.wireOp",EDGE,"E28.1.0.0")]});Q7=makeQuery(id+"F0.imprint","IMPRINT",FACE,{"disambiguationData":[TD([[makeQuery(id+"F0.imprint","IMPRINT",EDGE,{"disambiguationData":[TD([[subQ1,1.0]])],"derivedFrom":subQ0}),1.0]])]});}
            var Q8;
            {var subQ0=sQuery(id+"F0.wireOp",EDGE,"E1.2.1.0");var subQ1=makeQuery(id+"F0.imprint","INTERSECT",VERTEX,{"derivedFrom":[subQ0,sQuery(id+"F0.wireOp",EDGE,"E28.1.1.1")]});Q8=makeQuery(id+"F0.imprint","IMPRINT",FACE,{"disambiguationData":[TD([[makeQuery(id+"F0.imprint","IMPRINT",EDGE,{"disambiguationData":[TD([[subQ1,1.0]])],"derivedFrom":subQ0}),1.0]])]});}
            var Q9;
            {var subQ0=sQuery(id+"F0.wireOp",EDGE,"E1.3.0.0");var subQ1=makeQuery(id+"F0.imprint","INTERSECT",VERTEX,{"derivedFrom":[subQ0,sQuery(id+"F0.wireOp",EDGE,"E28.2.0.0")]});Q9=makeQuery(id+"F0.imprint","IMPRINT",FACE,{"disambiguationData":[TD([[makeQuery(id+"F0.imprint","IMPRINT",EDGE,{"disambiguationData":[TD([[subQ1,1.0]])],"derivedFrom":subQ0}),1.0]])]});}
            var Q10;
            {var subQ0=sQuery(id+"F0.wireOp",EDGE,"E1.3.1.0");var subQ1=makeQuery(id+"F0.imprint","INTERSECT",VERTEX,{"derivedFrom":[subQ0,sQuery(id+"F0.wireOp",EDGE,"E28.2.1.1")]});Q10=makeQuery(id+"F0.imprint","IMPRINT",FACE,{"disambiguationData":[TD([[makeQuery(id+"F0.imprint","IMPRINT",EDGE,{"disambiguationData":[TD([[subQ1,1.0]])],"derivedFrom":subQ0}),1.0]])]});}
            var Q11;
            {var subQ0=sQuery(id+"F0.wireOp",EDGE,"E1.4.0.0");var subQ1=makeQuery(id+"F0.imprint","INTERSECT",VERTEX,{"derivedFrom":[subQ0,sQuery(id+"F0.wireOp",EDGE,"E30.0.3.0")]});Q11=makeQuery(id+"F0.imprint","IMPRINT",FACE,{"disambiguationData":[TD([[makeQuery(id+"F0.imprint","IMPRINT",EDGE,{"disambiguationData":[TD([[subQ1,1.0]])],"derivedFrom":subQ0}),1.0]])]});}
            var Q12;
            {var subQ0=sQuery(id+"F0.wireOp",EDGE,"E1.4.1.0");var subQ1=makeQuery(id+"F0.imprint","INTERSECT",VERTEX,{"derivedFrom":[subQ0,sQuery(id+"F0.wireOp",EDGE,"E30.4.3.1")]});Q12=makeQuery(id+"F0.imprint","IMPRINT",FACE,{"disambiguationData":[TD([[makeQuery(id+"F0.imprint","IMPRINT",EDGE,{"disambiguationData":[TD([[subQ1,1.0]])],"derivedFrom":subQ0}),1.0]])]});}
            var Q13;
            {var subQ0=sQuery(id+"F0.wireOp",EDGE,"E1.5.0.0");var subQ1=makeQuery(id+"F0.imprint","INTERSECT",VERTEX,{"derivedFrom":[subQ0,sQuery(id+"F0.wireOp",EDGE,"E30.0.4.0")]});Q13=makeQuery(id+"F0.imprint","IMPRINT",FACE,{"disambiguationData":[TD([[makeQuery(id+"F0.imprint","IMPRINT",EDGE,{"disambiguationData":[TD([[subQ1,1.0]])],"derivedFrom":subQ0}),1.0]])]});}
            var Q14;
            {var subQ0=sQuery(id+"F0.wireOp",EDGE,"E1.5.1.0");var subQ1=makeQuery(id+"F0.imprint","INTERSECT",VERTEX,{"derivedFrom":[subQ0,sQuery(id+"F0.wireOp",EDGE,"E30.4.4.1")]});Q14=makeQuery(id+"F0.imprint","IMPRINT",FACE,{"disambiguationData":[TD([[makeQuery(id+"F0.imprint","IMPRINT",EDGE,{"disambiguationData":[TD([[subQ1,1.0]])],"derivedFrom":subQ0}),1.0]])]});}
            var Q15;
            {var subQ0=sQuery(id+"F0.wireOp",EDGE,"E1.6.0.0");var subQ1=makeQuery(id+"F0.imprint","INTERSECT",VERTEX,{"derivedFrom":[subQ0,sQuery(id+"F0.wireOp",EDGE,"E30.0.5.0")]});Q15=makeQuery(id+"F0.imprint","IMPRINT",FACE,{"disambiguationData":[TD([[makeQuery(id+"F0.imprint","IMPRINT",EDGE,{"disambiguationData":[TD([[subQ1,1.0]])],"derivedFrom":subQ0}),1.0]])]});}
            var Q16;
            {var subQ0=sQuery(id+"F0.wireOp",EDGE,"E1.6.1.0");var subQ1=makeQuery(id+"F0.imprint","INTERSECT",VERTEX,{"derivedFrom":[subQ0,sQuery(id+"F0.wireOp",EDGE,"E30.4.5.1")]});Q16=makeQuery(id+"F0.imprint","IMPRINT",FACE,{"disambiguationData":[TD([[makeQuery(id+"F0.imprint","IMPRINT",EDGE,{"disambiguationData":[TD([[subQ1,1.0]])],"derivedFrom":subQ0}),1.0]])]});}
            var Q17;
            {var subQ0=sQuery(id+"F0.wireOp",EDGE,"E1.7.0.0");var subQ1=makeQuery(id+"F0.imprint","INTERSECT",VERTEX,{"derivedFrom":[subQ0,sQuery(id+"F0.wireOp",EDGE,"E30.0.6.0")]});Q17=makeQuery(id+"F0.imprint","IMPRINT",FACE,{"disambiguationData":[TD([[makeQuery(id+"F0.imprint","IMPRINT",EDGE,{"disambiguationData":[TD([[subQ1,1.0]])],"derivedFrom":subQ0}),1.0]])]});}
            var Q18;
            {var subQ0=sQuery(id+"F0.wireOp",EDGE,"E1.7.1.0");var subQ1=makeQuery(id+"F0.imprint","INTERSECT",VERTEX,{"derivedFrom":[subQ0,sQuery(id+"F0.wireOp",EDGE,"E30.4.6.1")]});Q18=makeQuery(id+"F0.imprint","IMPRINT",FACE,{"disambiguationData":[TD([[makeQuery(id+"F0.imprint","IMPRINT",EDGE,{"disambiguationData":[TD([[subQ1,1.0]])],"derivedFrom":subQ0}),1.0]])]});}
            var Q19;
            {var subQ0=sQuery(id+"F0.wireOp",EDGE,"E1.8.0.0");var subQ1=makeQuery(id+"F0.imprint","INTERSECT",VERTEX,{"derivedFrom":[subQ0,sQuery(id+"F0.wireOp",EDGE,"E30.0.7.0")]});Q19=makeQuery(id+"F0.imprint","IMPRINT",FACE,{"disambiguationData":[TD([[makeQuery(id+"F0.imprint","IMPRINT",EDGE,{"disambiguationData":[TD([[subQ1,1.0]])],"derivedFrom":subQ0}),1.0]])]});}
            var Q20;
            {var subQ0=sQuery(id+"F0.wireOp",EDGE,"E1.8.1.0");var subQ1=makeQuery(id+"F0.imprint","INTERSECT",VERTEX,{"derivedFrom":[subQ0,sQuery(id+"F0.wireOp",EDGE,"E30.4.7.1")]});Q20=makeQuery(id+"F0.imprint","IMPRINT",FACE,{"disambiguationData":[TD([[makeQuery(id+"F0.imprint","IMPRINT",EDGE,{"disambiguationData":[TD([[subQ1,1.0]])],"derivedFrom":subQ0}),1.0]])]});}
            var Q21;
            {var subQ0=sQuery(id+"F0.wireOp",EDGE,"E1.9.0.0");var subQ1=makeQuery(id+"F0.imprint","INTERSECT",VERTEX,{"derivedFrom":[subQ0,sQuery(id+"F0.wireOp",EDGE,"E30.0.8.0")]});Q21=makeQuery(id+"F0.imprint","IMPRINT",FACE,{"disambiguationData":[TD([[makeQuery(id+"F0.imprint","IMPRINT",EDGE,{"disambiguationData":[TD([[subQ1,1.0]])],"derivedFrom":subQ0}),1.0]])]});}
            var Q22;
            {var subQ0=sQuery(id+"F0.wireOp",EDGE,"E1.9.1.0");var subQ1=makeQuery(id+"F0.imprint","INTERSECT",VERTEX,{"derivedFrom":[subQ0,sQuery(id+"F0.wireOp",EDGE,"E30.4.8.1")]});Q22=makeQuery(id+"F0.imprint","IMPRINT",FACE,{"disambiguationData":[TD([[makeQuery(id+"F0.imprint","IMPRINT",EDGE,{"disambiguationData":[TD([[subQ1,1.0]])],"derivedFrom":subQ0}),1.0]])]});}
            var Q23;
            {var subQ0=sQuery(id+"F0.wireOp",EDGE,"E29.0.10.0");var subQ1=makeQuery(id+"F0.imprint","INTERSECT",VERTEX,{"derivedFrom":[subQ0,sQuery(id+"F0.wireOp",EDGE,"E30.0.9.0")]});Q23=makeQuery(id+"F0.imprint","IMPRINT",FACE,{"disambiguationData":[TD([[makeQuery(id+"F0.imprint","IMPRINT",EDGE,{"disambiguationData":[TD([[subQ1,1.0]])],"derivedFrom":subQ0}),1.0]])]});}
            var Q24;
            {var subQ0=sQuery(id+"F0.wireOp",EDGE,"E29.0.10.1");var subQ1=makeQuery(id+"F0.imprint","INTERSECT",VERTEX,{"derivedFrom":[subQ0,sQuery(id+"F0.wireOp",EDGE,"E30.4.9.1")]});Q24=makeQuery(id+"F0.imprint","IMPRINT",FACE,{"disambiguationData":[TD([[makeQuery(id+"F0.imprint","IMPRINT",EDGE,{"disambiguationData":[TD([[subQ1,1.0]])],"derivedFrom":subQ0}),1.0]])]});}
            var Q25;
            {var subQ0=sQuery(id+"F0.wireOp",EDGE,"E29.0.11.0");var subQ1=makeQuery(id+"F0.imprint","INTERSECT",VERTEX,{"derivedFrom":[subQ0,sQuery(id+"F0.wireOp",EDGE,"E30.0.10.0")]});Q25=makeQuery(id+"F0.imprint","IMPRINT",FACE,{"disambiguationData":[TD([[makeQuery(id+"F0.imprint","IMPRINT",EDGE,{"disambiguationData":[TD([[subQ1,1.0]])],"derivedFrom":subQ0}),1.0]])]});}
            var Q26;
            {var subQ0=sQuery(id+"F0.wireOp",EDGE,"E29.0.11.1");var subQ1=makeQuery(id+"F0.imprint","INTERSECT",VERTEX,{"derivedFrom":[subQ0,sQuery(id+"F0.wireOp",EDGE,"E30.4.10.1")]});Q26=makeQuery(id+"F0.imprint","IMPRINT",FACE,{"disambiguationData":[TD([[makeQuery(id+"F0.imprint","IMPRINT",EDGE,{"disambiguationData":[TD([[subQ1,1.0]])],"derivedFrom":subQ0}),1.0]])]});}
            var Q27;
            {var subQ0=sQuery(id+"F0.wireOp",EDGE,"E29.0.12.0");var subQ1=makeQuery(id+"F0.imprint","INTERSECT",VERTEX,{"derivedFrom":[subQ0,sQuery(id+"F0.wireOp",EDGE,"E30.0.11.0")]});Q27=makeQuery(id+"F0.imprint","IMPRINT",FACE,{"disambiguationData":[TD([[makeQuery(id+"F0.imprint","IMPRINT",EDGE,{"disambiguationData":[TD([[subQ1,1.0]])],"derivedFrom":subQ0}),1.0]])]});}
            var Q28;
            {var subQ0=sQuery(id+"F0.wireOp",EDGE,"E29.0.12.1");var subQ1=makeQuery(id+"F0.imprint","INTERSECT",VERTEX,{"derivedFrom":[subQ0,sQuery(id+"F0.wireOp",EDGE,"E30.4.11.1")]});Q28=makeQuery(id+"F0.imprint","IMPRINT",FACE,{"disambiguationData":[TD([[makeQuery(id+"F0.imprint","IMPRINT",EDGE,{"disambiguationData":[TD([[subQ1,1.0]])],"derivedFrom":subQ0}),1.0]])]});}
            var Q29;
            {var subQ0=sQuery(id+"F0.wireOp",EDGE,"E29.0.13.0");var subQ1=makeQuery(id+"F0.imprint","INTERSECT",VERTEX,{"derivedFrom":[subQ0,sQuery(id+"F0.wireOp",EDGE,"E30.0.12.0")]});Q29=makeQuery(id+"F0.imprint","IMPRINT",FACE,{"disambiguationData":[TD([[makeQuery(id+"F0.imprint","IMPRINT",EDGE,{"disambiguationData":[TD([[subQ1,1.0]])],"derivedFrom":subQ0}),1.0]])]});}
            var Q30;
            {var subQ0=sQuery(id+"F0.wireOp",EDGE,"E29.0.13.1");var subQ1=makeQuery(id+"F0.imprint","INTERSECT",VERTEX,{"derivedFrom":[subQ0,sQuery(id+"F0.wireOp",EDGE,"E30.4.12.1")]});Q30=makeQuery(id+"F0.imprint","IMPRINT",FACE,{"disambiguationData":[TD([[makeQuery(id+"F0.imprint","IMPRINT",EDGE,{"disambiguationData":[TD([[subQ1,1.0]])],"derivedFrom":subQ0}),1.0]])]});}
            var Q31;
            {var subQ0=sQuery(id+"F0.wireOp",EDGE,"E29.0.14.0");var subQ1=makeQuery(id+"F0.imprint","INTERSECT",VERTEX,{"derivedFrom":[subQ0,sQuery(id+"F0.wireOp",EDGE,"E30.0.13.0")]});Q31=makeQuery(id+"F0.imprint","IMPRINT",FACE,{"disambiguationData":[TD([[makeQuery(id+"F0.imprint","IMPRINT",EDGE,{"disambiguationData":[TD([[subQ1,1.0]])],"derivedFrom":subQ0}),1.0]])]});}
            var Q32;
            {var subQ0=sQuery(id+"F0.wireOp",EDGE,"E29.0.14.1");var subQ1=makeQuery(id+"F0.imprint","INTERSECT",VERTEX,{"derivedFrom":[subQ0,sQuery(id+"F0.wireOp",EDGE,"E30.4.13.1")]});Q32=makeQuery(id+"F0.imprint","IMPRINT",FACE,{"disambiguationData":[TD([[makeQuery(id+"F0.imprint","IMPRINT",EDGE,{"disambiguationData":[TD([[subQ1,1.0]])],"derivedFrom":subQ0}),1.0]])]});}
            var Q33;
            {var subQ0=sQuery(id+"F0.wireOp",EDGE,"E29.0.15.0");var subQ1=makeQuery(id+"F0.imprint","INTERSECT",VERTEX,{"derivedFrom":[subQ0,sQuery(id+"F0.wireOp",EDGE,"E30.0.14.0")]});Q33=makeQuery(id+"F0.imprint","IMPRINT",FACE,{"disambiguationData":[TD([[makeQuery(id+"F0.imprint","IMPRINT",EDGE,{"disambiguationData":[TD([[subQ1,1.0]])],"derivedFrom":subQ0}),1.0]])]});}
            var Q34;
            {var subQ0=sQuery(id+"F0.wireOp",EDGE,"E29.0.15.1");var subQ1=makeQuery(id+"F0.imprint","INTERSECT",VERTEX,{"derivedFrom":[subQ0,sQuery(id+"F0.wireOp",EDGE,"E30.4.14.1")]});Q34=makeQuery(id+"F0.imprint","IMPRINT",FACE,{"disambiguationData":[TD([[makeQuery(id+"F0.imprint","IMPRINT",EDGE,{"disambiguationData":[TD([[subQ1,1.0]])],"derivedFrom":subQ0}),1.0]])]});}
            var Q35;
            {var subQ0=sQuery(id+"F0.wireOp",EDGE,"E29.0.16.0");var subQ1=makeQuery(id+"F0.imprint","INTERSECT",VERTEX,{"derivedFrom":[subQ0,sQuery(id+"F0.wireOp",EDGE,"E30.0.15.0")]});Q35=makeQuery(id+"F0.imprint","IMPRINT",FACE,{"disambiguationData":[TD([[makeQuery(id+"F0.imprint","IMPRINT",EDGE,{"disambiguationData":[TD([[subQ1,1.0]])],"derivedFrom":subQ0}),1.0]])]});}
            var Q36;
            {var subQ0=sQuery(id+"F0.wireOp",EDGE,"E29.0.16.1");var subQ1=makeQuery(id+"F0.imprint","INTERSECT",VERTEX,{"derivedFrom":[subQ0,sQuery(id+"F0.wireOp",EDGE,"E30.4.15.1")]});Q36=makeQuery(id+"F0.imprint","IMPRINT",FACE,{"disambiguationData":[TD([[makeQuery(id+"F0.imprint","IMPRINT",EDGE,{"disambiguationData":[TD([[subQ1,1.0]])],"derivedFrom":subQ0}),1.0]])]});}
            var Q37;
            {var subQ0=sQuery(id+"F0.wireOp",EDGE,"E29.0.17.0");var subQ1=makeQuery(id+"F0.imprint","INTERSECT",VERTEX,{"derivedFrom":[subQ0,sQuery(id+"F0.wireOp",EDGE,"E30.0.16.0")]});Q37=makeQuery(id+"F0.imprint","IMPRINT",FACE,{"disambiguationData":[TD([[makeQuery(id+"F0.imprint","IMPRINT",EDGE,{"disambiguationData":[TD([[subQ1,1.0]])],"derivedFrom":subQ0}),1.0]])]});}
            var Q38;
            {var subQ0=sQuery(id+"F0.wireOp",EDGE,"E29.0.17.1");var subQ1=makeQuery(id+"F0.imprint","INTERSECT",VERTEX,{"derivedFrom":[subQ0,sQuery(id+"F0.wireOp",EDGE,"E30.4.16.1")]});Q38=makeQuery(id+"F0.imprint","IMPRINT",FACE,{"disambiguationData":[TD([[makeQuery(id+"F0.imprint","IMPRINT",EDGE,{"disambiguationData":[TD([[subQ1,1.0]])],"derivedFrom":subQ0}),1.0]])]});}
            var Q39;
            {var subQ0=sQuery(id+"F0.wireOp",EDGE,"E29.0.18.0");var subQ1=makeQuery(id+"F0.imprint","INTERSECT",VERTEX,{"derivedFrom":[subQ0,sQuery(id+"F0.wireOp",EDGE,"E30.0.17.0")]});Q39=makeQuery(id+"F0.imprint","IMPRINT",FACE,{"disambiguationData":[TD([[makeQuery(id+"F0.imprint","IMPRINT",EDGE,{"disambiguationData":[TD([[subQ1,1.0]])],"derivedFrom":subQ0}),1.0]])]});}
            var Q40;
            {var subQ0=sQuery(id+"F0.wireOp",EDGE,"E29.0.18.1");var subQ1=makeQuery(id+"F0.imprint","INTERSECT",VERTEX,{"derivedFrom":[subQ0,sQuery(id+"F0.wireOp",EDGE,"E30.4.17.1")]});Q40=makeQuery(id+"F0.imprint","IMPRINT",FACE,{"disambiguationData":[TD([[makeQuery(id+"F0.imprint","IMPRINT",EDGE,{"disambiguationData":[TD([[subQ1,1.0]])],"derivedFrom":subQ0}),1.0]])]});}
            var Q41;
            {var subQ0=sQuery(id+"F0.wireOp",EDGE,"E29.0.19.0");var subQ1=makeQuery(id+"F0.imprint","INTERSECT",VERTEX,{"derivedFrom":[subQ0,sQuery(id+"F0.wireOp",EDGE,"E30.0.18.0")]});Q41=makeQuery(id+"F0.imprint","IMPRINT",FACE,{"disambiguationData":[TD([[makeQuery(id+"F0.imprint","IMPRINT",EDGE,{"disambiguationData":[TD([[subQ1,1.0]])],"derivedFrom":subQ0}),1.0]])]});}
            var Q42;
            {var subQ0=sQuery(id+"F0.wireOp",EDGE,"E29.0.19.1");var subQ1=makeQuery(id+"F0.imprint","INTERSECT",VERTEX,{"derivedFrom":[subQ0,sQuery(id+"F0.wireOp",EDGE,"E30.4.18.1")]});Q42=makeQuery(id+"F0.imprint","IMPRINT",FACE,{"disambiguationData":[TD([[makeQuery(id+"F0.imprint","IMPRINT",EDGE,{"disambiguationData":[TD([[subQ1,-1.0]])],"derivedFrom":subQ0}),1.0]])]});}
            var Q43;
            {var subQ5=sQuery(id+"F0.wireOp",EDGE,"E27");Q43=makeQuery(id+"F0.imprint","IMPRINT",FACE,{"disambiguationData":[TD([[makeQuery(id+"F0.imprint","IMPRINT",EDGE,{"derivedFrom":subQ5}),-1.0]])]});}
            var Q44;
            {var subQ48=sQuery(id+"F0.wireOp",EDGE,"E27");Q44=makeQuery(id+"F0.imprint","IMPRINT",FACE,{"disambiguationData":[TD([[makeQuery(id+"F0.imprint","IMPRINT",EDGE,{"derivedFrom":subQ48}),1.0]])]});}
            var Q45;
            {var subQ82=sQuery(id+"F0.wireOp",EDGE,"E26");Q45=makeQuery(id+"F0.imprint","IMPRINT",FACE,{"disambiguationData":[TD([[makeQuery(id+"F0.imprint","IMPRINT",EDGE,{"derivedFrom":subQ82}),-1.0]])]});}
            var Q46;
            {var subQ0=sQuery(id+"F0.wireOp",EDGE,"E28.0.1.0");Q46=makeQuery(id+"F0.imprint","IMPRINT",FACE,{"disambiguationData":[TD([[makeQuery(id+"F0.imprint","IMPRINT",EDGE,{"derivedFrom":subQ0}),1.0]])]});}
            var Q47;
            Q47=makeQuery(id+"F0.imprint","IMPRINT",FACE,{"disambiguationData":[TD([[makeQuery(id+"F0.imprint","IMPRINT",EDGE,{"derivedFrom":sQuery(id+"F0.wireOp",EDGE,"E28.1.0.0")}),1.0]])]});
            var Q48;
            Q48=makeQuery(id+"F0.imprint","IMPRINT",FACE,{"disambiguationData":[TD([[makeQuery(id+"F0.imprint","IMPRINT",EDGE,{"derivedFrom":sQuery(id+"F0.wireOp",EDGE,"E28.1.1.0")}),1.0]])]});
            var Q49;
            Q49=makeQuery(id+"F0.imprint","IMPRINT",FACE,{"disambiguationData":[TD([[makeQuery(id+"F0.imprint","IMPRINT",EDGE,{"derivedFrom":sQuery(id+"F0.wireOp",EDGE,"E28.2.0.0")}),1.0]])]});
            var Q50;
            Q50=makeQuery(id+"F0.imprint","IMPRINT",FACE,{"disambiguationData":[TD([[makeQuery(id+"F0.imprint","IMPRINT",EDGE,{"derivedFrom":sQuery(id+"F0.wireOp",EDGE,"E28.2.1.0")}),1.0]])]});
            var Q51;
            Q51=makeQuery(id+"F0.imprint","IMPRINT",FACE,{"disambiguationData":[TD([[makeQuery(id+"F0.imprint","IMPRINT",EDGE,{"derivedFrom":sQuery(id+"F0.wireOp",EDGE,"E30.0.3.0")}),1.0]])]});
            var Q52;
            Q52=makeQuery(id+"F0.imprint","IMPRINT",FACE,{"disambiguationData":[TD([[makeQuery(id+"F0.imprint","IMPRINT",EDGE,{"derivedFrom":sQuery(id+"F0.wireOp",EDGE,"E30.0.3.1")}),1.0]])]});
            var Q53;
            Q53=makeQuery(id+"F0.imprint","IMPRINT",FACE,{"disambiguationData":[TD([[makeQuery(id+"F0.imprint","IMPRINT",EDGE,{"derivedFrom":sQuery(id+"F0.wireOp",EDGE,"E30.0.4.0")}),1.0]])]});
            var Q54;
            Q54=makeQuery(id+"F0.imprint","IMPRINT",FACE,{"disambiguationData":[TD([[makeQuery(id+"F0.imprint","IMPRINT",EDGE,{"derivedFrom":sQuery(id+"F0.wireOp",EDGE,"E30.0.4.1")}),1.0]])]});
            var Q55;
            Q55=makeQuery(id+"F0.imprint","IMPRINT",FACE,{"disambiguationData":[TD([[makeQuery(id+"F0.imprint","IMPRINT",EDGE,{"derivedFrom":sQuery(id+"F0.wireOp",EDGE,"E30.0.5.0")}),1.0]])]});
            var Q56;
            Q56=makeQuery(id+"F0.imprint","IMPRINT",FACE,{"disambiguationData":[TD([[makeQuery(id+"F0.imprint","IMPRINT",EDGE,{"derivedFrom":sQuery(id+"F0.wireOp",EDGE,"E30.0.5.1")}),1.0]])]});
            var Q57;
            Q57=makeQuery(id+"F0.imprint","IMPRINT",FACE,{"disambiguationData":[TD([[makeQuery(id+"F0.imprint","IMPRINT",EDGE,{"derivedFrom":sQuery(id+"F0.wireOp",EDGE,"E30.0.6.0")}),1.0]])]});
            var Q58;
            Q58=makeQuery(id+"F0.imprint","IMPRINT",FACE,{"disambiguationData":[TD([[makeQuery(id+"F0.imprint","IMPRINT",EDGE,{"derivedFrom":sQuery(id+"F0.wireOp",EDGE,"E30.0.6.1")}),1.0]])]});
            var Q59;
            Q59=makeQuery(id+"F0.imprint","IMPRINT",FACE,{"disambiguationData":[TD([[makeQuery(id+"F0.imprint","IMPRINT",EDGE,{"derivedFrom":sQuery(id+"F0.wireOp",EDGE,"E30.0.7.0")}),1.0]])]});
            var Q60;
            Q60=makeQuery(id+"F0.imprint","IMPRINT",FACE,{"disambiguationData":[TD([[makeQuery(id+"F0.imprint","IMPRINT",EDGE,{"derivedFrom":sQuery(id+"F0.wireOp",EDGE,"E30.0.7.1")}),1.0]])]});
            var Q61;
            Q61=makeQuery(id+"F0.imprint","IMPRINT",FACE,{"disambiguationData":[TD([[makeQuery(id+"F0.imprint","IMPRINT",EDGE,{"derivedFrom":sQuery(id+"F0.wireOp",EDGE,"E30.0.8.0")}),1.0]])]});
            var Q62;
            Q62=makeQuery(id+"F0.imprint","IMPRINT",FACE,{"disambiguationData":[TD([[makeQuery(id+"F0.imprint","IMPRINT",EDGE,{"derivedFrom":sQuery(id+"F0.wireOp",EDGE,"E30.0.8.1")}),1.0]])]});
            var Q63;
            Q63=makeQuery(id+"F0.imprint","IMPRINT",FACE,{"disambiguationData":[TD([[makeQuery(id+"F0.imprint","IMPRINT",EDGE,{"derivedFrom":sQuery(id+"F0.wireOp",EDGE,"E30.0.9.0")}),1.0]])]});
            var Q64;
            Q64=makeQuery(id+"F0.imprint","IMPRINT",FACE,{"disambiguationData":[TD([[makeQuery(id+"F0.imprint","IMPRINT",EDGE,{"derivedFrom":sQuery(id+"F0.wireOp",EDGE,"E30.0.9.1")}),1.0]])]});
            var Q65;
            Q65=makeQuery(id+"F0.imprint","IMPRINT",FACE,{"disambiguationData":[TD([[makeQuery(id+"F0.imprint","IMPRINT",EDGE,{"derivedFrom":sQuery(id+"F0.wireOp",EDGE,"E30.0.10.0")}),1.0]])]});
            var Q66;
            Q66=makeQuery(id+"F0.imprint","IMPRINT",FACE,{"disambiguationData":[TD([[makeQuery(id+"F0.imprint","IMPRINT",EDGE,{"derivedFrom":sQuery(id+"F0.wireOp",EDGE,"E30.0.10.1")}),1.0]])]});
            var Q67;
            Q67=makeQuery(id+"F0.imprint","IMPRINT",FACE,{"disambiguationData":[TD([[makeQuery(id+"F0.imprint","IMPRINT",EDGE,{"derivedFrom":sQuery(id+"F0.wireOp",EDGE,"E30.0.11.0")}),1.0]])]});
            var Q68;
            Q68=makeQuery(id+"F0.imprint","IMPRINT",FACE,{"disambiguationData":[TD([[makeQuery(id+"F0.imprint","IMPRINT",EDGE,{"derivedFrom":sQuery(id+"F0.wireOp",EDGE,"E30.0.11.1")}),1.0]])]});
            var Q69;
            Q69=makeQuery(id+"F0.imprint","IMPRINT",FACE,{"disambiguationData":[TD([[makeQuery(id+"F0.imprint","IMPRINT",EDGE,{"derivedFrom":sQuery(id+"F0.wireOp",EDGE,"E30.0.12.0")}),1.0]])]});
            var Q70;
            Q70=makeQuery(id+"F0.imprint","IMPRINT",FACE,{"disambiguationData":[TD([[makeQuery(id+"F0.imprint","IMPRINT",EDGE,{"derivedFrom":sQuery(id+"F0.wireOp",EDGE,"E30.0.12.1")}),1.0]])]});
            var Q71;
            Q71=makeQuery(id+"F0.imprint","IMPRINT",FACE,{"disambiguationData":[TD([[makeQuery(id+"F0.imprint","IMPRINT",EDGE,{"derivedFrom":sQuery(id+"F0.wireOp",EDGE,"E30.0.13.0")}),1.0]])]});
            var Q72;
            Q72=makeQuery(id+"F0.imprint","IMPRINT",FACE,{"disambiguationData":[TD([[makeQuery(id+"F0.imprint","IMPRINT",EDGE,{"derivedFrom":sQuery(id+"F0.wireOp",EDGE,"E30.0.13.1")}),1.0]])]});
            var Q73;
            Q73=makeQuery(id+"F0.imprint","IMPRINT",FACE,{"disambiguationData":[TD([[makeQuery(id+"F0.imprint","IMPRINT",EDGE,{"derivedFrom":sQuery(id+"F0.wireOp",EDGE,"E30.0.14.0")}),1.0]])]});
            var Q74;
            Q74=makeQuery(id+"F0.imprint","IMPRINT",FACE,{"disambiguationData":[TD([[makeQuery(id+"F0.imprint","IMPRINT",EDGE,{"derivedFrom":sQuery(id+"F0.wireOp",EDGE,"E30.0.14.1")}),1.0]])]});
            var Q75;
            Q75=makeQuery(id+"F0.imprint","IMPRINT",FACE,{"disambiguationData":[TD([[makeQuery(id+"F0.imprint","IMPRINT",EDGE,{"derivedFrom":sQuery(id+"F0.wireOp",EDGE,"E30.0.15.0")}),1.0]])]});
            var Q76;
            Q76=makeQuery(id+"F0.imprint","IMPRINT",FACE,{"disambiguationData":[TD([[makeQuery(id+"F0.imprint","IMPRINT",EDGE,{"derivedFrom":sQuery(id+"F0.wireOp",EDGE,"E30.0.15.1")}),1.0]])]});
            var Q77;
            Q77=makeQuery(id+"F0.imprint","IMPRINT",FACE,{"disambiguationData":[TD([[makeQuery(id+"F0.imprint","IMPRINT",EDGE,{"derivedFrom":sQuery(id+"F0.wireOp",EDGE,"E30.0.16.0")}),1.0]])]});
            var Q78;
            Q78=makeQuery(id+"F0.imprint","IMPRINT",FACE,{"disambiguationData":[TD([[makeQuery(id+"F0.imprint","IMPRINT",EDGE,{"derivedFrom":sQuery(id+"F0.wireOp",EDGE,"E30.0.16.1")}),1.0]])]});
            var Q79;
            Q79=makeQuery(id+"F0.imprint","IMPRINT",FACE,{"disambiguationData":[TD([[makeQuery(id+"F0.imprint","IMPRINT",EDGE,{"derivedFrom":sQuery(id+"F0.wireOp",EDGE,"E30.0.17.0")}),1.0]])]});
            var Q80;
            Q80=makeQuery(id+"F0.imprint","IMPRINT",FACE,{"disambiguationData":[TD([[makeQuery(id+"F0.imprint","IMPRINT",EDGE,{"derivedFrom":sQuery(id+"F0.wireOp",EDGE,"E30.0.17.1")}),1.0]])]});
            var Q81;
            Q81=makeQuery(id+"F0.imprint","IMPRINT",FACE,{"disambiguationData":[TD([[makeQuery(id+"F0.imprint","IMPRINT",EDGE,{"derivedFrom":sQuery(id+"F0.wireOp",EDGE,"E30.0.18.0")}),1.0]])]});
            var Q82;
            Q82=makeQuery(id+"F0.imprint","IMPRINT",FACE,{"disambiguationData":[TD([[makeQuery(id+"F0.imprint","IMPRINT",EDGE,{"derivedFrom":sQuery(id+"F0.wireOp",EDGE,"E30.0.18.1")}),1.0]])]});
            extrude(context, id + "F3", {"entities" : qUnion([Q0, Q1, Q2, Q3, Q4, Q5, Q6, Q7, Q8, Q9, Q10, Q11, Q12, Q13, Q14, Q15, Q16, Q17, Q18, Q19, Q20, Q21, Q22, Q23, Q24, Q25, Q26, Q27, Q28, Q29, Q30, Q31, Q32, Q33, Q34, Q35, Q36, Q37, Q38, Q39, Q40, Q41, Q42, Q43, Q44, Q45, Q46, Q47, Q48, Q49, Q50, Q51, Q52, Q53, Q54, Q55, Q56, Q57, Q58, Q59, Q60, Q61, Q62, Q63, Q64, Q65, Q66, Q67, Q68, Q69, Q70, Q71, Q72, Q73, Q74, Q75, Q76, Q77, Q78, Q79, Q80, Q81, Q82]), "operationType" : NewBodyOperationType.ADD, "oppositeDirection" : true, "depth" : 3.2 * mm, "offsetDistance" : 25 * mm});
        }
        {
            var Q0;
            Q0=makeQuery(id+"F1.opExtrude","CAP_EDGE",EDGE,{"disambiguationData":[OSD([sQuery(id+"F0.wireOp",EDGE,"E8")])],"isStart":false});
            fillet(context, id + "F4", {"entities" : qUnion([Q0]), "tangentPropagation" : true, "radius" : .8 * mm, "defaultsChanged" : true, "vertexSettings" : [], "allowEdgeOverflow" : false});
        }
    });
